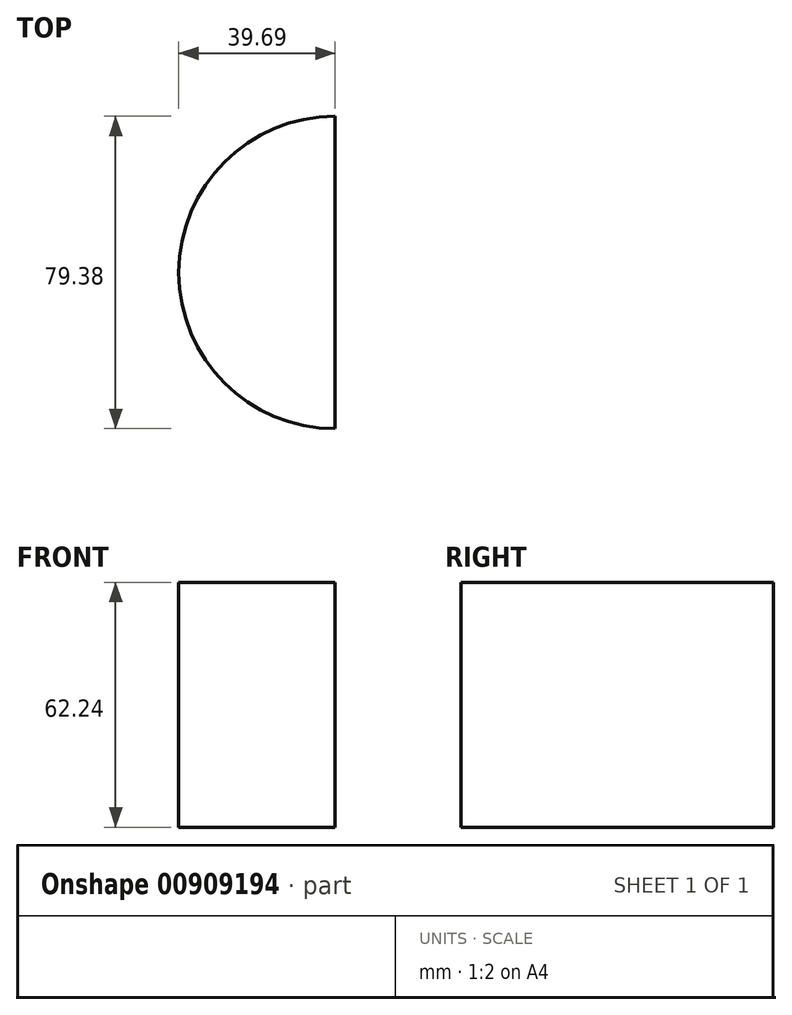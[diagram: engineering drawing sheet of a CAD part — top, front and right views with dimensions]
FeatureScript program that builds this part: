
annotation { "Feature Type Name" : "Feature", "Feature Type Description" : "" }
export const myFeature = defineFeature(function(context is Context, id is Id, definition is map)
    precondition{}
    {
        {
            var Q0;
            Q0=qCreatedBy(makeId("Top.planeOp"),FACE);
            var sketch = newSketch(context, id + "F0", { "sketchPlane" : qUnion([Q0])});
            skCircle(sketch, "E0", {"center": v(0, 0) * mm, "radius": 39.69 * mm});
            skCircle(sketch, "E1", {"center": v(0, 0) * mm, "radius": 59.07 * mm});
            skLineSegment(sketch, "E2", {"start": v(0, 66.93) * mm, "end": v(0, -68.13) * mm});
            skSolve(sketch);
        }
        {
            var Q0;
            {var subQ0=sQuery(id+"F0.wireOp",EDGE,"E2");var subQ1=sQuery(id+"F0.wireOp",EDGE,"E0");var subQ2=makeQuery(id+"F0.imprint","INTERSECT",VERTEX,{"disambiguationData":[OD(0.0)],"derivedFrom":[subQ1,subQ0]});Q0=makeQuery(id+"F0.imprint","IMPRINT",FACE,{"disambiguationData":[TD([[makeQuery(id+"F0.imprint","IMPRINT",EDGE,{"disambiguationData":[TD([[subQ2,-1.0]])],"derivedFrom":subQ1}),1.0]])]});}
            extrude(context, id + "F1", {"entities" : qUnion([Q0]), "endBound" : BoundingType.SYMMETRIC, "oppositeDirection" : true, "depth" : 62.23 * mm, "offsetDistance" : 25.4 * mm});
        }
    });
